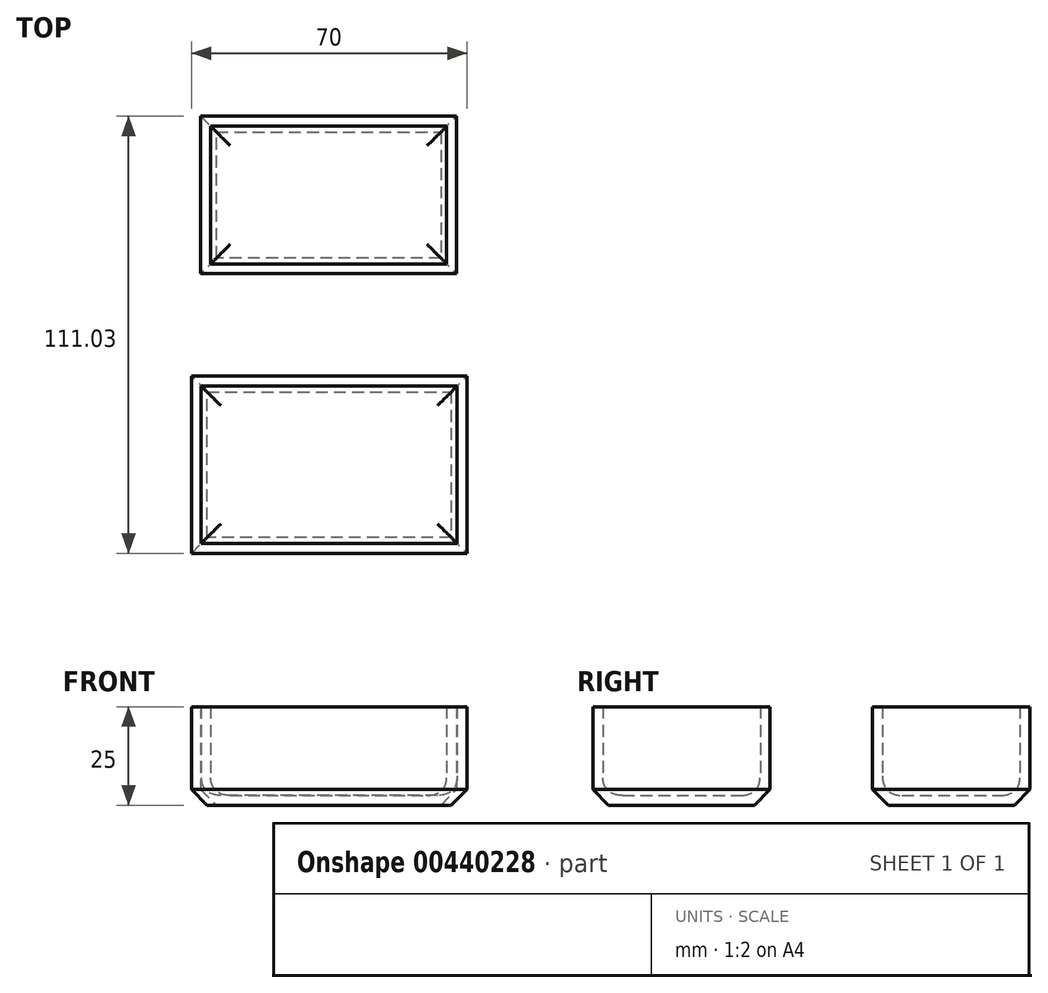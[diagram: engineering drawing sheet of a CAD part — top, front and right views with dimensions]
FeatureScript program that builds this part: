
annotation { "Feature Type Name" : "Feature", "Feature Type Description" : "" }
export const myFeature = defineFeature(function(context is Context, id is Id, definition is map)
    precondition{}
    {
        {
            var Q0;
            Q0=qCreatedBy(makeId("Top.planeOp"),FACE);
            var sketch = newSketch(context, id + "F0", { "sketchPlane" : qUnion([Q0])});
            skLineSegment(sketch, "E0", {"start": v(44.3, -17) * mm, "end": v(44.3, -62) * mm});
            skLineSegment(sketch, "E1", {"start": v(44.3, -62) * mm, "end": v(-25.7, -62) * mm});
            skLineSegment(sketch, "E2", {"start": v(-25.7, -62) * mm, "end": v(-25.7, -17) * mm});
            skLineSegment(sketch, "E3", {"start": v(-25.7, -17) * mm, "end": v(44.3, -17) * mm});
            skSolve(sketch);
        }
        {
            var Q0;
            Q0=makeQuery(id+"F0.imprint","IMPRINT",FACE,{"disambiguationData":[TD([[makeQuery(id+"F0.imprint","IMPRINT",EDGE,{"derivedFrom":sQuery(id+"F0.wireOp",EDGE,"E0")}),-1.0]])]});
            extrude(context, id + "F1", {"entities" : qUnion([Q0]), "depth" : 25 * mm});
        }
        {
            var Q0;
            Q0=makeQuery(id+"F1.opExtrude","CAP_FACE",FACE,{"disambiguationData":[OSD([sQuery(id+"F0.wireOp",EDGE,"E0"),sQuery(id+"F0.wireOp",EDGE,"E1"),sQuery(id+"F0.wireOp",EDGE,"E2"),sQuery(id+"F0.wireOp",EDGE,"E3")])],"isStart":false});
            shell(context, id + "F2", {"entities" : qUnion([Q0]), "thickness" : 2.5 * mm});
        }
        {
            var Q0;
            {var subQ0=sQuery(id+"F0.wireOp",EDGE,"E2");Q0=makeQuery(id+"F2.opShell","OFFSET_EDGE",EDGE,{"disambiguationData":[OSD([subQ0]),TDD([makeQuery(id+"F1.opExtrude","CAP_EDGE",EDGE,{"disambiguationData":[OSD([subQ0])],"isStart":true})])]});}
            var Q1;
            {var subQ0=sQuery(id+"F0.wireOp",EDGE,"E3");Q1=makeQuery(id+"F2.opShell","OFFSET_EDGE",EDGE,{"disambiguationData":[OSD([subQ0]),TDD([makeQuery(id+"F1.opExtrude","CAP_EDGE",EDGE,{"disambiguationData":[OSD([subQ0])],"isStart":true})])]});}
            var Q2;
            {var subQ0=sQuery(id+"F0.wireOp",EDGE,"E0");Q2=makeQuery(id+"F2.opShell","OFFSET_EDGE",EDGE,{"disambiguationData":[OSD([subQ0]),TDD([makeQuery(id+"F1.opExtrude","CAP_EDGE",EDGE,{"disambiguationData":[OSD([subQ0])],"isStart":true})])]});}
            var Q3;
            {var subQ0=sQuery(id+"F0.wireOp",EDGE,"E1");Q3=makeQuery(id+"F2.opShell","OFFSET_EDGE",EDGE,{"disambiguationData":[OSD([subQ0]),TDD([makeQuery(id+"F1.opExtrude","CAP_EDGE",EDGE,{"disambiguationData":[OSD([subQ0])],"isStart":true})])]});}
            fillet(context, id + "F3", {"entities" : qUnion([Q0, Q1, Q2, Q3]), "radius" : 5 * mm, "tangentPropagation" : true, "rho" : 0.5, "crossSection" : FilletCrossSection.CONIC, "allowEdgeOverflow" : false});
        }
        {
            var Q0;
            Q0=makeQuery(id+"F1.opExtrude","CAP_EDGE",EDGE,{"disambiguationData":[OSD([sQuery(id+"F0.wireOp",EDGE,"E1")])],"isStart":true});
            var Q1;
            Q1=makeQuery(id+"F1.opExtrude","CAP_EDGE",EDGE,{"disambiguationData":[OSD([sQuery(id+"F0.wireOp",EDGE,"E2")])],"isStart":true});
            var Q2;
            Q2=makeQuery(id+"F1.opExtrude","CAP_EDGE",EDGE,{"disambiguationData":[OSD([sQuery(id+"F0.wireOp",EDGE,"E0")])],"isStart":true});
            var Q3;
            Q3=makeQuery(id+"F1.opExtrude","CAP_EDGE",EDGE,{"disambiguationData":[OSD([sQuery(id+"F0.wireOp",EDGE,"E3")])],"isStart":true});
            chamfer(context, id + "F4", {"entities" : qUnion([Q0, Q1, Q2, Q3]), "width" : 4 * mm, "tangentPropagation" : true});
        }
        {
            var Q0;
            Q0=qCreatedBy(makeId("Top.planeOp"),FACE);
            var sketch = newSketch(context, id + "F5", { "sketchPlane" : qUnion([Q0])});
            skLineSegment(sketch, "E4.bottom", {"start": v(-23.34, 49.03) * mm, "end": v(41.66, 49.03) * mm});
            skLineSegment(sketch, "E4.top", {"start": v(-23.34, 9.03) * mm, "end": v(41.66, 9.03) * mm});
            skLineSegment(sketch, "E4.left", {"start": v(-23.34, 49.03) * mm, "end": v(-23.34, 9.03) * mm});
            skLineSegment(sketch, "E4.right", {"start": v(41.66, 49.03) * mm, "end": v(41.66, 9.03) * mm});
            skSolve(sketch);
        }
        {
            var Q0;
            Q0 = qSketchRegion(id + "F5", true);
            extrude(context, id + "F6", {"entities" : qUnion([Q0]), "depth" : 25 * mm});
        }
        {
            var Q0;
            Q0=makeQuery(id+"F6.opExtrude","CAP_FACE",FACE,{"disambiguationData":[OSD([sQuery(id+"F5.wireOp",EDGE,"E4.bottom"),sQuery(id+"F5.wireOp",EDGE,"E4.top"),sQuery(id+"F5.wireOp",EDGE,"E4.left"),sQuery(id+"F5.wireOp",EDGE,"E4.right")])],"isStart":false});
            shell(context, id + "F7", {"entities" : qUnion([Q0]), "thickness" : 2.5 * mm});
        }
        {
            var Q0;
            {var subQ0=sQuery(id+"F5.wireOp",EDGE,"E4.left");Q0=makeQuery(id+"F7.opShell","OFFSET_EDGE",EDGE,{"disambiguationData":[OSD([subQ0]),TDD([makeQuery(id+"F6.opExtrude","CAP_EDGE",EDGE,{"disambiguationData":[OSD([subQ0])],"isStart":true})])]});}
            var Q1;
            {var subQ0=sQuery(id+"F5.wireOp",EDGE,"E4.top");Q1=makeQuery(id+"F7.opShell","OFFSET_EDGE",EDGE,{"disambiguationData":[OSD([subQ0]),TDD([makeQuery(id+"F6.opExtrude","CAP_EDGE",EDGE,{"disambiguationData":[OSD([subQ0])],"isStart":true})])]});}
            var Q2;
            {var subQ0=sQuery(id+"F5.wireOp",EDGE,"E4.bottom");Q2=makeQuery(id+"F7.opShell","OFFSET_EDGE",EDGE,{"disambiguationData":[OSD([subQ0]),TDD([makeQuery(id+"F6.opExtrude","CAP_EDGE",EDGE,{"disambiguationData":[OSD([subQ0])],"isStart":true})])]});}
            var Q3;
            {var subQ0=sQuery(id+"F5.wireOp",EDGE,"E4.right");Q3=makeQuery(id+"F7.opShell","OFFSET_EDGE",EDGE,{"disambiguationData":[OSD([subQ0]),TDD([makeQuery(id+"F6.opExtrude","CAP_EDGE",EDGE,{"disambiguationData":[OSD([subQ0])],"isStart":true})])]});}
            fillet(context, id + "F8", {"entities" : qUnion([Q0, Q1, Q2, Q3]), "radius" : 5 * mm, "tangentPropagation" : true, "rho" : 0.5, "crossSection" : FilletCrossSection.CONIC, "allowEdgeOverflow" : false});
        }
        {
            var Q0;
            Q0=makeQuery(id+"F6.opExtrude","CAP_EDGE",EDGE,{"disambiguationData":[OSD([sQuery(id+"F5.wireOp",EDGE,"E4.top")])],"isStart":true});
            var Q1;
            Q1=makeQuery(id+"F6.opExtrude","CAP_EDGE",EDGE,{"disambiguationData":[OSD([sQuery(id+"F5.wireOp",EDGE,"E4.left")])],"isStart":true});
            var Q2;
            Q2=makeQuery(id+"F6.opExtrude","CAP_EDGE",EDGE,{"disambiguationData":[OSD([sQuery(id+"F5.wireOp",EDGE,"E4.bottom")])],"isStart":true});
            var Q3;
            Q3=makeQuery(id+"F6.opExtrude","CAP_EDGE",EDGE,{"disambiguationData":[OSD([sQuery(id+"F5.wireOp",EDGE,"E4.right")])],"isStart":true});
            chamfer(context, id + "F9", {"entities" : qUnion([Q0, Q1, Q2, Q3]), "width" : 4 * mm, "tangentPropagation" : true});
        }
    });
